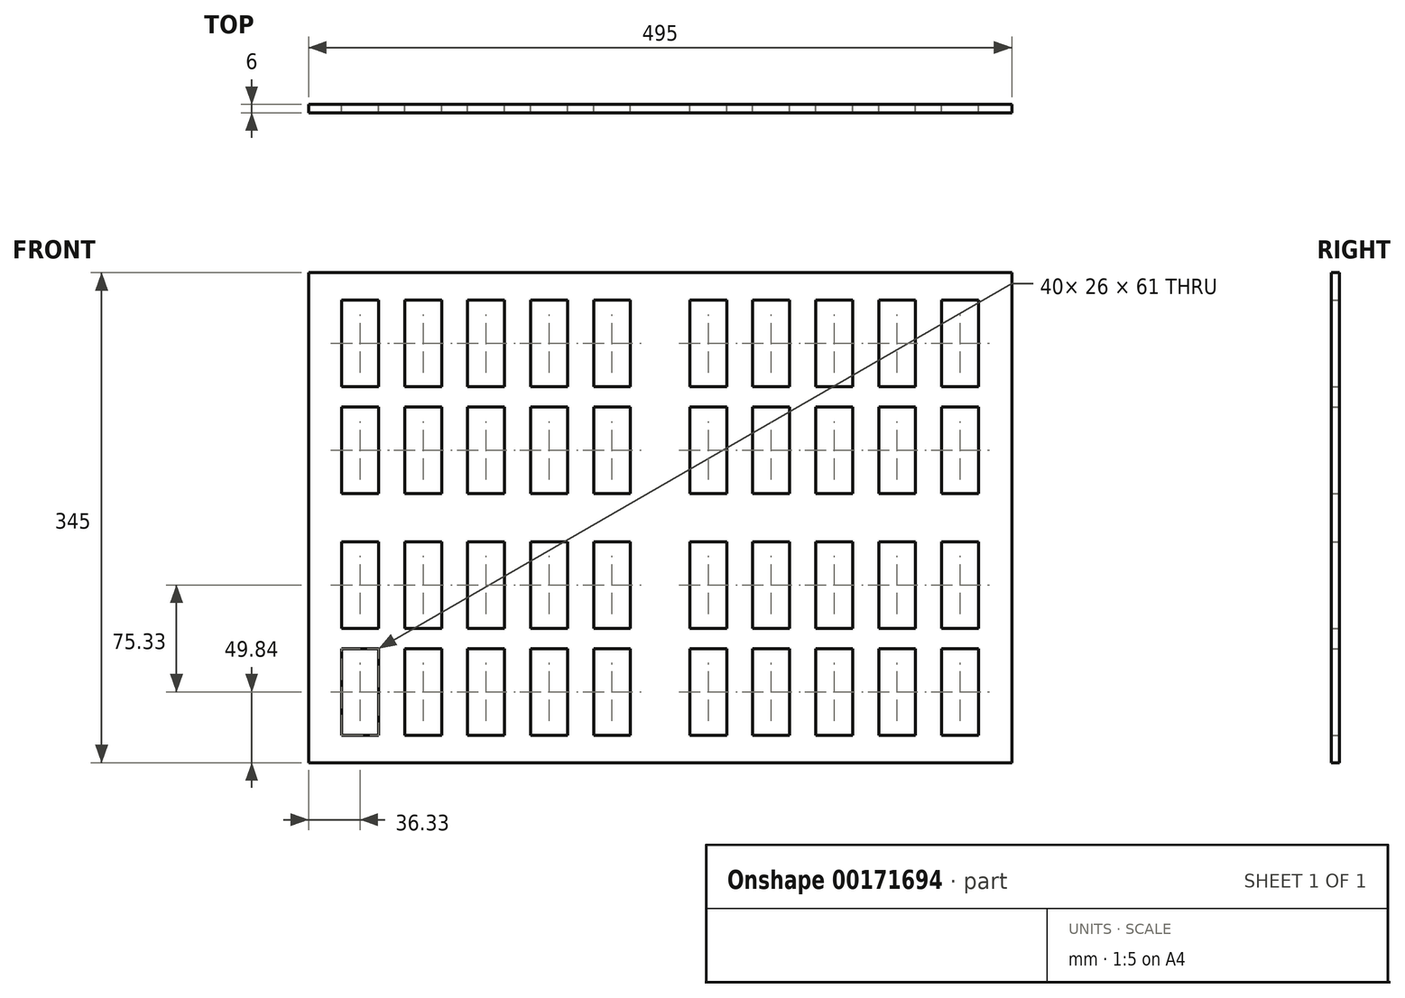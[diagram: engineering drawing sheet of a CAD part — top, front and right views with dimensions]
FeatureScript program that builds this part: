
annotation { "Feature Type Name" : "Feature", "Feature Type Description" : "" }
export const myFeature = defineFeature(function(context is Context, id is Id, definition is map)
    precondition{}
    {
        {
            var Q0;
            Q0=qCreatedBy(makeId("Front.planeOp"),FACE);
            var sketch = newSketch(context, id + "F0", { "sketchPlane" : qUnion([Q0])});
            skLineSegment(sketch, "E0.bottom", {"start": v(223.5, -176.5) * mm, "end": v(-231.5, -176.5) * mm});
            skLineSegment(sketch, "E0.top", {"start": v(227.5, 168.5) * mm, "end": v(-227.5, 168.5) * mm});
            skLineSegment(sketch, "E0.left", {"start": v(243.5, -156.5) * mm, "end": v(243.5, 148.5) * mm});
            skLineSegment(sketch, "E0.right", {"start": v(-251.5, -152.5) * mm, "end": v(-251.5, 152.5) * mm});
            skPoint(sketch, "E1.visualSharp", {"position": v(-251.5, 168.5) * mm});
            skPoint(sketch, "E2.visualSharp", {"position": v(243.5, 168.5) * mm});
            skPoint(sketch, "E3.visualSharp", {"position": v(243.5, -176.5) * mm});
            skPoint(sketch, "E4.visualSharp", {"position": v(-251.5, -176.5) * mm});
            skLineSegment(sketch, "E5", {"start": v(-251.5, 152.5) * mm, "end": v(-251.5, 168.5) * mm});
            skLineSegment(sketch, "E6", {"start": v(-251.5, 168.5) * mm, "end": v(-227.5, 168.5) * mm});
            skLineSegment(sketch, "E7", {"start": v(-251.5, -176.5) * mm, "end": v(-251.5, -152.5) * mm});
            skLineSegment(sketch, "E8", {"start": v(-251.5, -176.5) * mm, "end": v(-231.5, -176.5) * mm});
            skLineSegment(sketch, "E9", {"start": v(243.5, -156.5) * mm, "end": v(243.5, -176.5) * mm});
            skLineSegment(sketch, "E10", {"start": v(223.5, -176.5) * mm, "end": v(243.5, -176.5) * mm});
            skLineSegment(sketch, "E11", {"start": v(227.5, 168.5) * mm, "end": v(243.5, 168.5) * mm});
            skLineSegment(sketch, "E12", {"start": v(243.5, 148.5) * mm, "end": v(243.5, 168.5) * mm});
            skPoint(sketch, "E13.0.1.2", {"position": v(-247.5, 2.5) * mm});
            skLineSegment(sketch, "E14.bottom", {"start": v(-228.17, 149.17) * mm, "end": v(-202.17, 149.17) * mm});
            skLineSegment(sketch, "E14.top", {"start": v(-228.17, 88.17) * mm, "end": v(-202.17, 88.17) * mm});
            skLineSegment(sketch, "E14.left", {"start": v(-228.17, 149.17) * mm, "end": v(-228.17, 88.17) * mm});
            skLineSegment(sketch, "E14.right", {"start": v(-202.17, 149.17) * mm, "end": v(-202.17, 88.17) * mm});
            skLineSegment(sketch, "E15.0.1.0", {"start": v(-228.17, 12.84) * mm, "end": v(-202.17, 12.84) * mm});
            skLineSegment(sketch, "E15.0.1.1", {"start": v(-202.17, 73.84) * mm, "end": v(-202.17, 12.84) * mm});
            skLineSegment(sketch, "E15.0.1.2", {"start": v(-228.17, 73.84) * mm, "end": v(-228.17, 12.84) * mm});
            skLineSegment(sketch, "E15.0.1.3", {"start": v(-228.17, 73.84) * mm, "end": v(-202.17, 73.84) * mm});
            skLineSegment(sketch, "E15.1.0.0", {"start": v(-183.84, 88.17) * mm, "end": v(-157.84, 88.17) * mm});
            skLineSegment(sketch, "E15.1.0.1", {"start": v(-157.84, 149.17) * mm, "end": v(-157.84, 88.17) * mm});
            skLineSegment(sketch, "E15.1.0.2", {"start": v(-183.84, 149.17) * mm, "end": v(-183.84, 88.17) * mm});
            skLineSegment(sketch, "E15.1.0.3", {"start": v(-183.84, 149.17) * mm, "end": v(-157.84, 149.17) * mm});
            skLineSegment(sketch, "E15.1.1.0", {"start": v(-183.84, 12.84) * mm, "end": v(-157.84, 12.84) * mm});
            skLineSegment(sketch, "E15.1.1.1", {"start": v(-157.84, 73.84) * mm, "end": v(-157.84, 12.84) * mm});
            skLineSegment(sketch, "E15.1.1.2", {"start": v(-183.84, 73.84) * mm, "end": v(-183.84, 12.84) * mm});
            skLineSegment(sketch, "E15.1.1.3", {"start": v(-183.84, 73.84) * mm, "end": v(-157.84, 73.84) * mm});
            skLineSegment(sketch, "E15.2.0.0", {"start": v(-139.5, 88.17) * mm, "end": v(-113.5, 88.17) * mm});
            skLineSegment(sketch, "E15.2.0.1", {"start": v(-113.5, 149.17) * mm, "end": v(-113.5, 88.17) * mm});
            skLineSegment(sketch, "E15.2.0.2", {"start": v(-139.5, 149.17) * mm, "end": v(-139.5, 88.17) * mm});
            skLineSegment(sketch, "E15.2.0.3", {"start": v(-139.5, 149.17) * mm, "end": v(-113.5, 149.17) * mm});
            skLineSegment(sketch, "E15.2.1.0", {"start": v(-139.5, 12.84) * mm, "end": v(-113.5, 12.84) * mm});
            skLineSegment(sketch, "E15.2.1.1", {"start": v(-113.5, 73.84) * mm, "end": v(-113.5, 12.84) * mm});
            skLineSegment(sketch, "E15.2.1.2", {"start": v(-139.5, 73.84) * mm, "end": v(-139.5, 12.84) * mm});
            skLineSegment(sketch, "E15.2.1.3", {"start": v(-139.5, 73.84) * mm, "end": v(-113.5, 73.84) * mm});
            skLineSegment(sketch, "E15.3.0.0", {"start": v(-95.18, 88.17) * mm, "end": v(-69.18, 88.17) * mm});
            skLineSegment(sketch, "E15.3.0.1", {"start": v(-69.18, 149.17) * mm, "end": v(-69.18, 88.17) * mm});
            skLineSegment(sketch, "E15.3.0.2", {"start": v(-95.18, 149.17) * mm, "end": v(-95.18, 88.17) * mm});
            skLineSegment(sketch, "E15.3.0.3", {"start": v(-95.18, 149.17) * mm, "end": v(-69.18, 149.17) * mm});
            skLineSegment(sketch, "E15.3.1.0", {"start": v(-95.18, 12.84) * mm, "end": v(-69.18, 12.84) * mm});
            skLineSegment(sketch, "E15.3.1.1", {"start": v(-69.18, 73.84) * mm, "end": v(-69.18, 12.84) * mm});
            skLineSegment(sketch, "E15.3.1.2", {"start": v(-95.18, 73.84) * mm, "end": v(-95.18, 12.84) * mm});
            skLineSegment(sketch, "E15.3.1.3", {"start": v(-95.18, 73.84) * mm, "end": v(-69.18, 73.84) * mm});
            skLineSegment(sketch, "E15.4.0.0", {"start": v(-50.85, 88.17) * mm, "end": v(-24.85, 88.17) * mm});
            skLineSegment(sketch, "E15.4.0.1", {"start": v(-24.85, 149.17) * mm, "end": v(-24.85, 88.17) * mm});
            skLineSegment(sketch, "E15.4.0.2", {"start": v(-50.85, 149.17) * mm, "end": v(-50.85, 88.17) * mm});
            skLineSegment(sketch, "E15.4.0.3", {"start": v(-50.85, 149.17) * mm, "end": v(-24.85, 149.17) * mm});
            skLineSegment(sketch, "E15.4.1.0", {"start": v(-50.85, 12.84) * mm, "end": v(-24.85, 12.84) * mm});
            skLineSegment(sketch, "E15.4.1.1", {"start": v(-24.85, 73.84) * mm, "end": v(-24.85, 12.84) * mm});
            skLineSegment(sketch, "E15.4.1.2", {"start": v(-50.85, 73.84) * mm, "end": v(-50.85, 12.84) * mm});
            skLineSegment(sketch, "E15.4.1.3", {"start": v(-50.85, 73.84) * mm, "end": v(-24.85, 73.84) * mm});
            skLineSegment(sketch, "E15.direction1", {"start": v(-228.17, 88.17) * mm, "end": v(-183.84, 88.17) * mm, "construction": true});
            skLineSegment(sketch, "E15.direction2", {"start": v(-228.17, 88.17) * mm, "end": v(-228.17, 12.84) * mm, "construction": true});
            skLineSegment(sketch, "E16.0.1.0", {"start": v(-113.5, -20.83) * mm, "end": v(-113.5, -81.83) * mm});
            skLineSegment(sketch, "E16.0.1.1", {"start": v(-95.18, -81.83) * mm, "end": v(-69.18, -81.83) * mm});
            skLineSegment(sketch, "E16.0.1.2", {"start": v(-95.18, -20.83) * mm, "end": v(-95.18, -81.83) * mm});
            skLineSegment(sketch, "E16.0.1.3", {"start": v(-183.84, -96.16) * mm, "end": v(-183.84, -157.16) * mm});
            skLineSegment(sketch, "E16.0.1.4", {"start": v(-157.84, -20.83) * mm, "end": v(-157.84, -81.83) * mm});
            skLineSegment(sketch, "E16.0.1.5", {"start": v(-50.85, -81.83) * mm, "end": v(-24.85, -81.83) * mm});
            skLineSegment(sketch, "E16.0.1.6", {"start": v(-50.85, -96.16) * mm, "end": v(-50.85, -157.16) * mm});
            skLineSegment(sketch, "E16.0.1.7", {"start": v(-183.84, -20.83) * mm, "end": v(-183.84, -81.83) * mm});
            skLineSegment(sketch, "E16.0.1.8", {"start": v(-228.17, -81.83) * mm, "end": v(-228.17, -157.16) * mm, "construction": true});
            skLineSegment(sketch, "E16.0.1.9", {"start": v(-183.84, -20.83) * mm, "end": v(-157.84, -20.83) * mm});
            skLineSegment(sketch, "E16.0.1.10", {"start": v(-95.18, -157.16) * mm, "end": v(-69.18, -157.16) * mm});
            skLineSegment(sketch, "E16.0.1.11", {"start": v(-157.84, -96.16) * mm, "end": v(-157.84, -157.16) * mm});
            skLineSegment(sketch, "E16.0.1.12", {"start": v(-202.17, -20.83) * mm, "end": v(-202.17, -81.83) * mm});
            skLineSegment(sketch, "E16.0.1.13", {"start": v(-139.5, -20.83) * mm, "end": v(-113.5, -20.83) * mm});
            skLineSegment(sketch, "E16.0.1.14", {"start": v(-95.18, -20.83) * mm, "end": v(-69.18, -20.83) * mm});
            skLineSegment(sketch, "E16.0.1.15", {"start": v(-228.17, -20.83) * mm, "end": v(-228.17, -81.83) * mm});
            skLineSegment(sketch, "E16.0.1.16", {"start": v(-69.18, -96.16) * mm, "end": v(-69.18, -157.16) * mm});
            skLineSegment(sketch, "E16.0.1.17", {"start": v(-183.84, -157.16) * mm, "end": v(-157.84, -157.16) * mm});
            skLineSegment(sketch, "E16.0.1.18", {"start": v(-50.85, -20.83) * mm, "end": v(-24.85, -20.83) * mm});
            skLineSegment(sketch, "E16.0.1.19", {"start": v(-228.17, -20.83) * mm, "end": v(-202.17, -20.83) * mm});
            skLineSegment(sketch, "E16.0.1.20", {"start": v(-113.5, -96.16) * mm, "end": v(-113.5, -157.16) * mm});
            skLineSegment(sketch, "E16.0.1.21", {"start": v(-69.18, -20.83) * mm, "end": v(-69.18, -81.83) * mm});
            skLineSegment(sketch, "E16.0.1.22", {"start": v(-139.5, -20.83) * mm, "end": v(-139.5, -81.83) * mm});
            skLineSegment(sketch, "E16.0.1.23", {"start": v(-139.5, -96.16) * mm, "end": v(-113.5, -96.16) * mm});
            skLineSegment(sketch, "E16.0.1.24", {"start": v(-50.85, -20.83) * mm, "end": v(-50.85, -81.83) * mm});
            skLineSegment(sketch, "E16.0.1.25", {"start": v(-228.17, -81.83) * mm, "end": v(-183.84, -81.83) * mm, "construction": true});
            skLineSegment(sketch, "E16.0.1.26", {"start": v(-24.85, -20.83) * mm, "end": v(-24.85, -81.83) * mm});
            skLineSegment(sketch, "E16.0.1.27", {"start": v(-183.84, -81.83) * mm, "end": v(-157.84, -81.83) * mm});
            skLineSegment(sketch, "E16.0.1.28", {"start": v(-50.85, -96.16) * mm, "end": v(-24.85, -96.16) * mm});
            skLineSegment(sketch, "E16.0.1.29", {"start": v(-183.84, -96.16) * mm, "end": v(-157.84, -96.16) * mm});
            skLineSegment(sketch, "E16.0.1.30", {"start": v(-95.18, -96.16) * mm, "end": v(-69.18, -96.16) * mm});
            skLineSegment(sketch, "E16.0.1.31", {"start": v(-95.18, -96.16) * mm, "end": v(-95.18, -157.16) * mm});
            skLineSegment(sketch, "E16.0.1.32", {"start": v(-139.5, -81.83) * mm, "end": v(-113.5, -81.83) * mm});
            skLineSegment(sketch, "E16.0.1.33", {"start": v(-139.5, -96.16) * mm, "end": v(-139.5, -157.16) * mm});
            skLineSegment(sketch, "E16.0.1.34", {"start": v(-228.17, -157.16) * mm, "end": v(-202.17, -157.16) * mm});
            skLineSegment(sketch, "E16.0.1.35", {"start": v(-50.85, -157.16) * mm, "end": v(-24.85, -157.16) * mm});
            skLineSegment(sketch, "E16.0.1.36", {"start": v(-139.5, -157.16) * mm, "end": v(-113.5, -157.16) * mm});
            skLineSegment(sketch, "E16.0.1.37", {"start": v(-24.85, -96.16) * mm, "end": v(-24.85, -157.16) * mm});
            skLineSegment(sketch, "E16.0.1.38", {"start": v(-202.17, -96.16) * mm, "end": v(-202.17, -157.16) * mm});
            skLineSegment(sketch, "E16.0.1.39", {"start": v(-228.17, -81.83) * mm, "end": v(-202.17, -81.83) * mm});
            skLineSegment(sketch, "E16.0.1.40", {"start": v(-228.17, -96.16) * mm, "end": v(-228.17, -157.16) * mm});
            skLineSegment(sketch, "E16.0.1.41", {"start": v(-228.17, -96.16) * mm, "end": v(-202.17, -96.16) * mm});
            skLineSegment(sketch, "E16.1.0.0", {"start": v(131.5, 149.17) * mm, "end": v(131.5, 88.17) * mm});
            skLineSegment(sketch, "E16.1.0.1", {"start": v(149.82, 88.17) * mm, "end": v(175.82, 88.17) * mm});
            skLineSegment(sketch, "E16.1.0.2", {"start": v(149.82, 149.17) * mm, "end": v(149.82, 88.17) * mm});
            skLineSegment(sketch, "E16.1.0.3", {"start": v(61.16, 73.84) * mm, "end": v(61.16, 12.84) * mm});
            skLineSegment(sketch, "E16.1.0.4", {"start": v(87.16, 149.17) * mm, "end": v(87.16, 88.17) * mm});
            skLineSegment(sketch, "E16.1.0.5", {"start": v(194.15, 88.17) * mm, "end": v(220.15, 88.17) * mm});
            skLineSegment(sketch, "E16.1.0.6", {"start": v(194.15, 73.84) * mm, "end": v(194.15, 12.84) * mm});
            skLineSegment(sketch, "E16.1.0.7", {"start": v(61.16, 149.17) * mm, "end": v(61.16, 88.17) * mm});
            skLineSegment(sketch, "E16.1.0.8", {"start": v(16.83, 88.17) * mm, "end": v(16.83, 12.84) * mm, "construction": true});
            skLineSegment(sketch, "E16.1.0.9", {"start": v(61.16, 149.17) * mm, "end": v(87.16, 149.17) * mm});
            skLineSegment(sketch, "E16.1.0.10", {"start": v(149.82, 12.84) * mm, "end": v(175.82, 12.84) * mm});
            skLineSegment(sketch, "E16.1.0.11", {"start": v(87.16, 73.84) * mm, "end": v(87.16, 12.84) * mm});
            skLineSegment(sketch, "E16.1.0.12", {"start": v(42.83, 149.17) * mm, "end": v(42.83, 88.17) * mm});
            skLineSegment(sketch, "E16.1.0.13", {"start": v(105.5, 149.17) * mm, "end": v(131.5, 149.17) * mm});
            skLineSegment(sketch, "E16.1.0.14", {"start": v(149.82, 149.17) * mm, "end": v(175.82, 149.17) * mm});
            skLineSegment(sketch, "E16.1.0.15", {"start": v(16.83, 149.17) * mm, "end": v(16.83, 88.17) * mm});
            skLineSegment(sketch, "E16.1.0.16", {"start": v(175.82, 73.84) * mm, "end": v(175.82, 12.84) * mm});
            skLineSegment(sketch, "E16.1.0.17", {"start": v(61.16, 12.84) * mm, "end": v(87.16, 12.84) * mm});
            skLineSegment(sketch, "E16.1.0.18", {"start": v(194.15, 149.17) * mm, "end": v(220.15, 149.17) * mm});
            skLineSegment(sketch, "E16.1.0.19", {"start": v(16.83, 149.17) * mm, "end": v(42.83, 149.17) * mm});
            skLineSegment(sketch, "E16.1.0.20", {"start": v(131.5, 73.84) * mm, "end": v(131.5, 12.84) * mm});
            skLineSegment(sketch, "E16.1.0.21", {"start": v(175.82, 149.17) * mm, "end": v(175.82, 88.17) * mm});
            skLineSegment(sketch, "E16.1.0.22", {"start": v(105.5, 149.17) * mm, "end": v(105.5, 88.17) * mm});
            skLineSegment(sketch, "E16.1.0.23", {"start": v(105.5, 73.84) * mm, "end": v(131.5, 73.84) * mm});
            skLineSegment(sketch, "E16.1.0.24", {"start": v(194.15, 149.17) * mm, "end": v(194.15, 88.17) * mm});
            skLineSegment(sketch, "E16.1.0.25", {"start": v(16.83, 88.17) * mm, "end": v(61.16, 88.17) * mm, "construction": true});
            skLineSegment(sketch, "E16.1.0.26", {"start": v(220.15, 149.17) * mm, "end": v(220.15, 88.17) * mm});
            skLineSegment(sketch, "E16.1.0.27", {"start": v(61.16, 88.17) * mm, "end": v(87.16, 88.17) * mm});
            skLineSegment(sketch, "E16.1.0.28", {"start": v(194.15, 73.84) * mm, "end": v(220.15, 73.84) * mm});
            skLineSegment(sketch, "E16.1.0.29", {"start": v(61.16, 73.84) * mm, "end": v(87.16, 73.84) * mm});
            skLineSegment(sketch, "E16.1.0.30", {"start": v(149.82, 73.84) * mm, "end": v(175.82, 73.84) * mm});
            skLineSegment(sketch, "E16.1.0.31", {"start": v(149.82, 73.84) * mm, "end": v(149.82, 12.84) * mm});
            skLineSegment(sketch, "E16.1.0.32", {"start": v(105.5, 88.17) * mm, "end": v(131.5, 88.17) * mm});
            skLineSegment(sketch, "E16.1.0.33", {"start": v(105.5, 73.84) * mm, "end": v(105.5, 12.84) * mm});
            skLineSegment(sketch, "E16.1.0.34", {"start": v(16.83, 12.84) * mm, "end": v(42.83, 12.84) * mm});
            skLineSegment(sketch, "E16.1.0.35", {"start": v(194.15, 12.84) * mm, "end": v(220.15, 12.84) * mm});
            skLineSegment(sketch, "E16.1.0.36", {"start": v(105.5, 12.84) * mm, "end": v(131.5, 12.84) * mm});
            skLineSegment(sketch, "E16.1.0.37", {"start": v(220.15, 73.84) * mm, "end": v(220.15, 12.84) * mm});
            skLineSegment(sketch, "E16.1.0.38", {"start": v(42.83, 73.84) * mm, "end": v(42.83, 12.84) * mm});
            skLineSegment(sketch, "E16.1.0.39", {"start": v(16.83, 88.17) * mm, "end": v(42.83, 88.17) * mm});
            skLineSegment(sketch, "E16.1.0.40", {"start": v(16.83, 73.84) * mm, "end": v(16.83, 12.84) * mm});
            skLineSegment(sketch, "E16.1.0.41", {"start": v(16.83, 73.84) * mm, "end": v(42.83, 73.84) * mm});
            skLineSegment(sketch, "E16.1.1.0", {"start": v(131.5, -20.83) * mm, "end": v(131.5, -81.83) * mm});
            skLineSegment(sketch, "E16.1.1.1", {"start": v(149.82, -81.83) * mm, "end": v(175.82, -81.83) * mm});
            skLineSegment(sketch, "E16.1.1.2", {"start": v(149.82, -20.83) * mm, "end": v(149.82, -81.83) * mm});
            skLineSegment(sketch, "E16.1.1.3", {"start": v(61.16, -96.16) * mm, "end": v(61.16, -157.16) * mm});
            skLineSegment(sketch, "E16.1.1.4", {"start": v(87.16, -20.83) * mm, "end": v(87.16, -81.83) * mm});
            skLineSegment(sketch, "E16.1.1.5", {"start": v(194.15, -81.83) * mm, "end": v(220.15, -81.83) * mm});
            skLineSegment(sketch, "E16.1.1.6", {"start": v(194.15, -96.16) * mm, "end": v(194.15, -157.16) * mm});
            skLineSegment(sketch, "E16.1.1.7", {"start": v(61.16, -20.83) * mm, "end": v(61.16, -81.83) * mm});
            skLineSegment(sketch, "E16.1.1.8", {"start": v(16.83, -81.83) * mm, "end": v(16.83, -157.16) * mm, "construction": true});
            skLineSegment(sketch, "E16.1.1.9", {"start": v(61.16, -20.83) * mm, "end": v(87.16, -20.83) * mm});
            skLineSegment(sketch, "E16.1.1.10", {"start": v(149.82, -157.16) * mm, "end": v(175.82, -157.16) * mm});
            skLineSegment(sketch, "E16.1.1.11", {"start": v(87.16, -96.16) * mm, "end": v(87.16, -157.16) * mm});
            skLineSegment(sketch, "E16.1.1.12", {"start": v(42.83, -20.83) * mm, "end": v(42.83, -81.83) * mm});
            skLineSegment(sketch, "E16.1.1.13", {"start": v(105.5, -20.83) * mm, "end": v(131.5, -20.83) * mm});
            skLineSegment(sketch, "E16.1.1.14", {"start": v(149.82, -20.83) * mm, "end": v(175.82, -20.83) * mm});
            skLineSegment(sketch, "E16.1.1.15", {"start": v(16.83, -20.83) * mm, "end": v(16.83, -81.83) * mm});
            skLineSegment(sketch, "E16.1.1.16", {"start": v(175.82, -96.16) * mm, "end": v(175.82, -157.16) * mm});
            skLineSegment(sketch, "E16.1.1.17", {"start": v(61.16, -157.16) * mm, "end": v(87.16, -157.16) * mm});
            skLineSegment(sketch, "E16.1.1.18", {"start": v(194.15, -20.83) * mm, "end": v(220.15, -20.83) * mm});
            skLineSegment(sketch, "E16.1.1.19", {"start": v(16.83, -20.83) * mm, "end": v(42.83, -20.83) * mm});
            skLineSegment(sketch, "E16.1.1.20", {"start": v(131.5, -96.16) * mm, "end": v(131.5, -157.16) * mm});
            skLineSegment(sketch, "E16.1.1.21", {"start": v(175.82, -20.83) * mm, "end": v(175.82, -81.83) * mm});
            skLineSegment(sketch, "E16.1.1.22", {"start": v(105.5, -20.83) * mm, "end": v(105.5, -81.83) * mm});
            skLineSegment(sketch, "E16.1.1.23", {"start": v(105.5, -96.16) * mm, "end": v(131.5, -96.16) * mm});
            skLineSegment(sketch, "E16.1.1.24", {"start": v(194.15, -20.83) * mm, "end": v(194.15, -81.83) * mm});
            skLineSegment(sketch, "E16.1.1.25", {"start": v(16.83, -81.83) * mm, "end": v(61.16, -81.83) * mm, "construction": true});
            skLineSegment(sketch, "E16.1.1.26", {"start": v(220.15, -20.83) * mm, "end": v(220.15, -81.83) * mm});
            skLineSegment(sketch, "E16.1.1.27", {"start": v(61.16, -81.83) * mm, "end": v(87.16, -81.83) * mm});
            skLineSegment(sketch, "E16.1.1.28", {"start": v(194.15, -96.16) * mm, "end": v(220.15, -96.16) * mm});
            skLineSegment(sketch, "E16.1.1.29", {"start": v(61.16, -96.16) * mm, "end": v(87.16, -96.16) * mm});
            skLineSegment(sketch, "E16.1.1.30", {"start": v(149.82, -96.16) * mm, "end": v(175.82, -96.16) * mm});
            skLineSegment(sketch, "E16.1.1.31", {"start": v(149.82, -96.16) * mm, "end": v(149.82, -157.16) * mm});
            skLineSegment(sketch, "E16.1.1.32", {"start": v(105.5, -81.83) * mm, "end": v(131.5, -81.83) * mm});
            skLineSegment(sketch, "E16.1.1.33", {"start": v(105.5, -96.16) * mm, "end": v(105.5, -157.16) * mm});
            skLineSegment(sketch, "E16.1.1.34", {"start": v(16.83, -157.16) * mm, "end": v(42.83, -157.16) * mm});
            skLineSegment(sketch, "E16.1.1.35", {"start": v(194.15, -157.16) * mm, "end": v(220.15, -157.16) * mm});
            skLineSegment(sketch, "E16.1.1.36", {"start": v(105.5, -157.16) * mm, "end": v(131.5, -157.16) * mm});
            skLineSegment(sketch, "E16.1.1.37", {"start": v(220.15, -96.16) * mm, "end": v(220.15, -157.16) * mm});
            skLineSegment(sketch, "E16.1.1.38", {"start": v(42.83, -96.16) * mm, "end": v(42.83, -157.16) * mm});
            skLineSegment(sketch, "E16.1.1.39", {"start": v(16.83, -81.83) * mm, "end": v(42.83, -81.83) * mm});
            skLineSegment(sketch, "E16.1.1.40", {"start": v(16.83, -96.16) * mm, "end": v(16.83, -157.16) * mm});
            skLineSegment(sketch, "E16.1.1.41", {"start": v(16.83, -96.16) * mm, "end": v(42.83, -96.16) * mm});
            skLineSegment(sketch, "E16.direction1", {"start": v(-228.17, 12.84) * mm, "end": v(16.83, 12.84) * mm, "construction": true});
            skLineSegment(sketch, "E16.direction2", {"start": v(-228.17, 12.84) * mm, "end": v(-228.17, -157.16) * mm, "construction": true});
            skSolve(sketch);
        }
        {
            var Q0;
            Q0=qSketchRegion(id+"F0",true);
            extrude(context, id + "F1", {"entities" : qUnion([Q0]), "depth" : 6 * mm, "offsetDistance" : 25 * mm});
        }
    });
